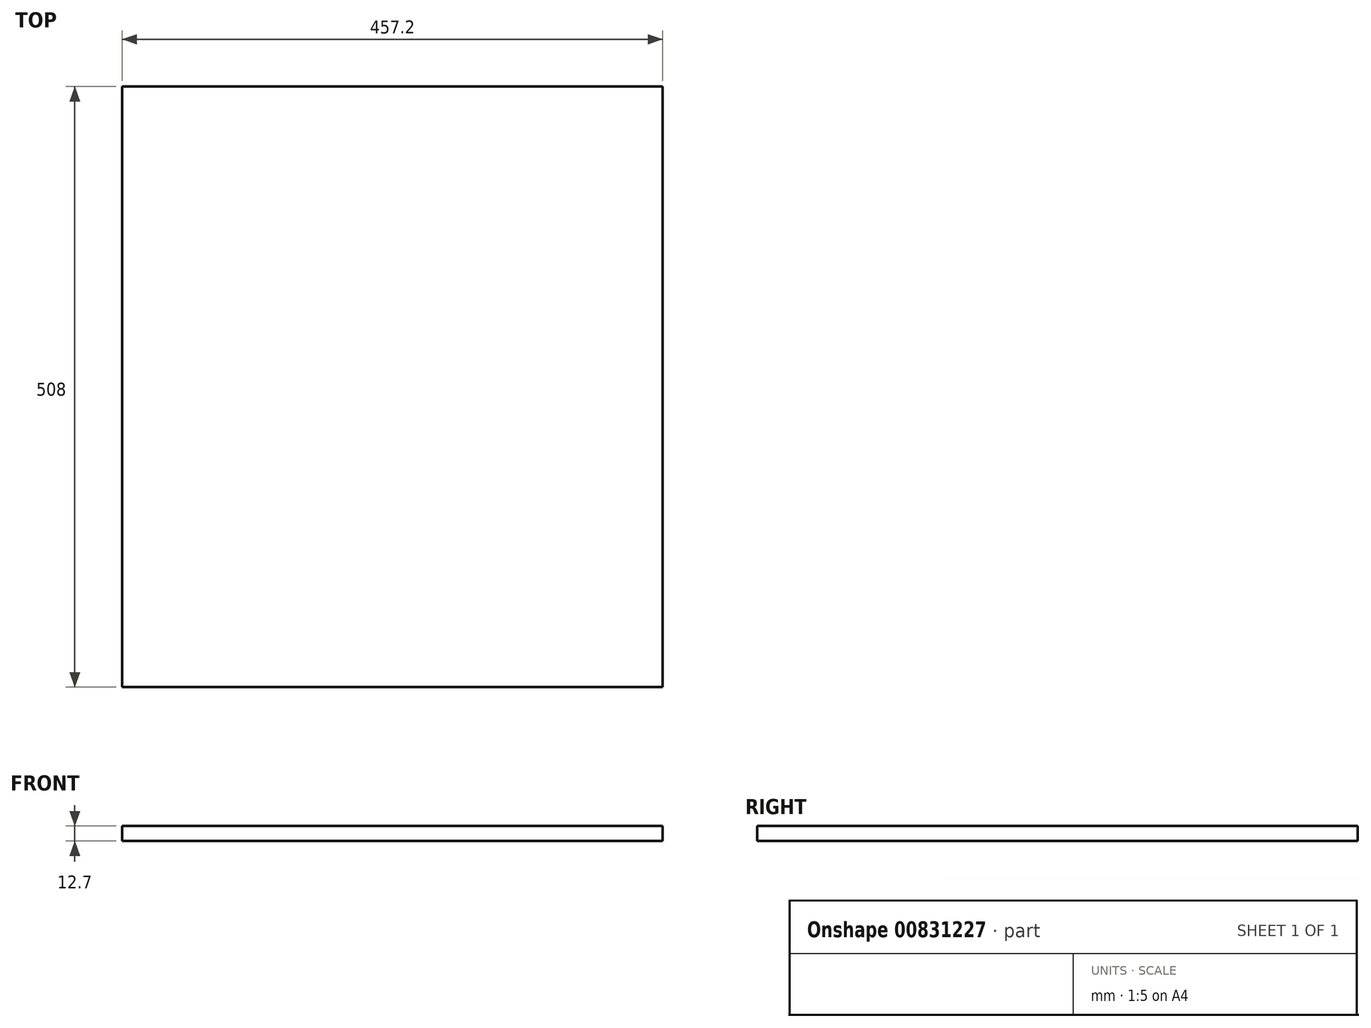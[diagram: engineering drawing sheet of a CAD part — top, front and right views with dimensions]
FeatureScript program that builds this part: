
annotation { "Feature Type Name" : "Feature", "Feature Type Description" : "" }
export const myFeature = defineFeature(function(context is Context, id is Id, definition is map)
    precondition{}
    {
        {
            var Q0;
            Q0=qCreatedBy(makeId("Top.planeOp"),FACE);
            var sketch = newSketch(context, id + "F0", { "sketchPlane" : qUnion([Q0])});
            skLineSegment(sketch, "E0.bottom", {"start": v(-238.87, 337.97) * mm, "end": v(218.33, 337.97) * mm});
            skLineSegment(sketch, "E0.top", {"start": v(-238.87, -170.03) * mm, "end": v(218.33, -170.03) * mm});
            skLineSegment(sketch, "E0.left", {"start": v(-238.87, 337.97) * mm, "end": v(-238.87, -170.03) * mm});
            skLineSegment(sketch, "E0.right", {"start": v(218.33, 337.97) * mm, "end": v(218.33, -170.03) * mm});
            skSolve(sketch);
        }
        {
            var Q0;
            Q0 = qSketchRegion(id + "F0", true);
            extrude(context, id + "F1", {"entities" : qUnion([Q0]), "depth" : 12.7 * mm, "offsetDistance" : 25.4 * mm});
        }
    });
